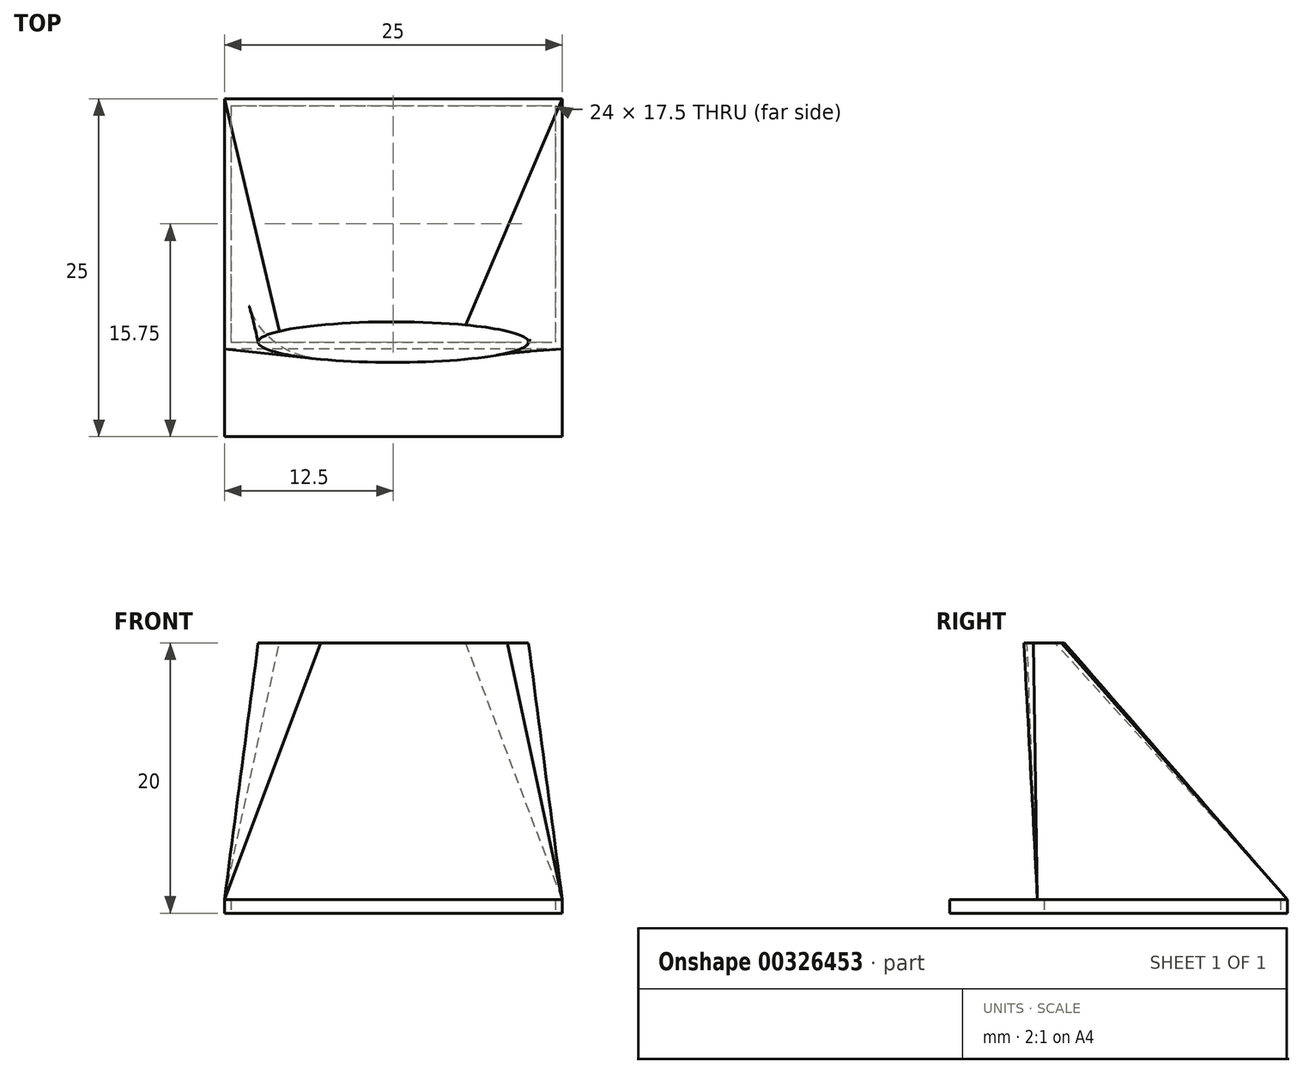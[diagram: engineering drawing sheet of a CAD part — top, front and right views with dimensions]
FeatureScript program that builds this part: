
annotation { "Feature Type Name" : "Feature", "Feature Type Description" : "" }
export const myFeature = defineFeature(function(context is Context, id is Id, definition is map)
    precondition{}
    {
        {
            var Q0;
            Q0=qCreatedBy(makeId("Top.planeOp"),FACE);
            var sketch = newSketch(context, id + "F0", { "sketchPlane" : qUnion([Q0])});
            skLineSegment(sketch, "E0.bottom", {"start": v(0, 0) * mm, "end": v(25, 0) * mm});
            skLineSegment(sketch, "E0.top", {"start": v(0, 25) * mm, "end": v(25, 25) * mm});
            skLineSegment(sketch, "E0.left", {"start": v(0, 0) * mm, "end": v(0, 25) * mm});
            skLineSegment(sketch, "E0.right", {"start": v(25, 0) * mm, "end": v(25, 25) * mm});
            skLineSegment(sketch, "E1.bottom", {"start": v(0.5, 24.5) * mm, "end": v(24.5, 24.5) * mm});
            skLineSegment(sketch, "E1.top", {"start": v(0.5, 7) * mm, "end": v(24.5, 7) * mm});
            skLineSegment(sketch, "E1.left", {"start": v(0.5, 24.5) * mm, "end": v(0.5, 7) * mm});
            skLineSegment(sketch, "E1.right", {"start": v(24.5, 24.5) * mm, "end": v(24.5, 7) * mm});
            skSolve(sketch);
        }
        {
            var Q0;
            Q0=makeQuery(id+"F0.imprint","IMPRINT",FACE,{"disambiguationData":[TD([[makeQuery(id+"F0.imprint","IMPRINT",EDGE,{"derivedFrom":sQuery(id+"F0.wireOp",EDGE,"E0.bottom")}),1.0]])]});
            extrude(context, id + "F1", {"entities" : qUnion([Q0]), "depth" : 1 * mm});
        }
        {
            var Q0;
            Q0=qCreatedBy(makeId("Top.planeOp"),FACE);
            cPlane(context, id + "F2", {"entities" : qUnion([Q0]), "cplaneType" : CPlaneType.OFFSET, "offset" : 20 * mm, "width" : 152.4 * mm, "height" : 152.4 * mm});
        }
        {
            var Q0;
            Q0=qCreatedBy(id+"F2.planeOp",FACE);
            var sketch = newSketch(context, id + "F3", { "sketchPlane" : qUnion([Q0])});
            skEllipse(sketch, "E2", {"center": v(12.5, 7) * mm, "majorRadius": 10 * mm, "minorRadius": 1.5 * mm, "majorAxis": v(1, 0)});
            skSolve(sketch);
        }
        {
            var Q0;
            Q0=makeQuery(id+"F1.opExtrude","CAP_FACE",FACE,{"disambiguationData":[OSD([sQuery(id+"F0.wireOp",EDGE,"E0.bottom"),sQuery(id+"F0.wireOp",EDGE,"E0.top"),sQuery(id+"F0.wireOp",EDGE,"E0.left"),sQuery(id+"F0.wireOp",EDGE,"E0.right"),sQuery(id+"F0.wireOp",EDGE,"E1.bottom"),sQuery(id+"F0.wireOp",EDGE,"E1.top"),sQuery(id+"F0.wireOp",EDGE,"E1.left"),sQuery(id+"F0.wireOp",EDGE,"E1.right")])],"isStart":false});
            var sketch = newSketch(context, id + "F4", { "sketchPlane" : qUnion([Q0])});
            skLineSegment(sketch, "E3.bottom", {"start": v(25, 25) * mm, "end": v(0, 25) * mm});
            skLineSegment(sketch, "E3.top", {"start": v(25, 6.5) * mm, "end": v(0, 6.5) * mm});
            skLineSegment(sketch, "E3.left", {"start": v(25, 25) * mm, "end": v(25, 6.5) * mm});
            skLineSegment(sketch, "E3.right", {"start": v(0, 25) * mm, "end": v(0, 6.5) * mm});
            skSolve(sketch);
        }
        {
            var Q0;
            Q0 = qSketchRegion(id + "F4", true);
            var Q1;
            Q1 = qSketchRegion(id + "F3", true);
            loft(context, id + "F5", {"sheetProfilesArray" : [{ "sheetProfileEntities" : qUnion([Q0]) }, { "sheetProfileEntities" : qUnion([Q1]) }]});
        }
    });
